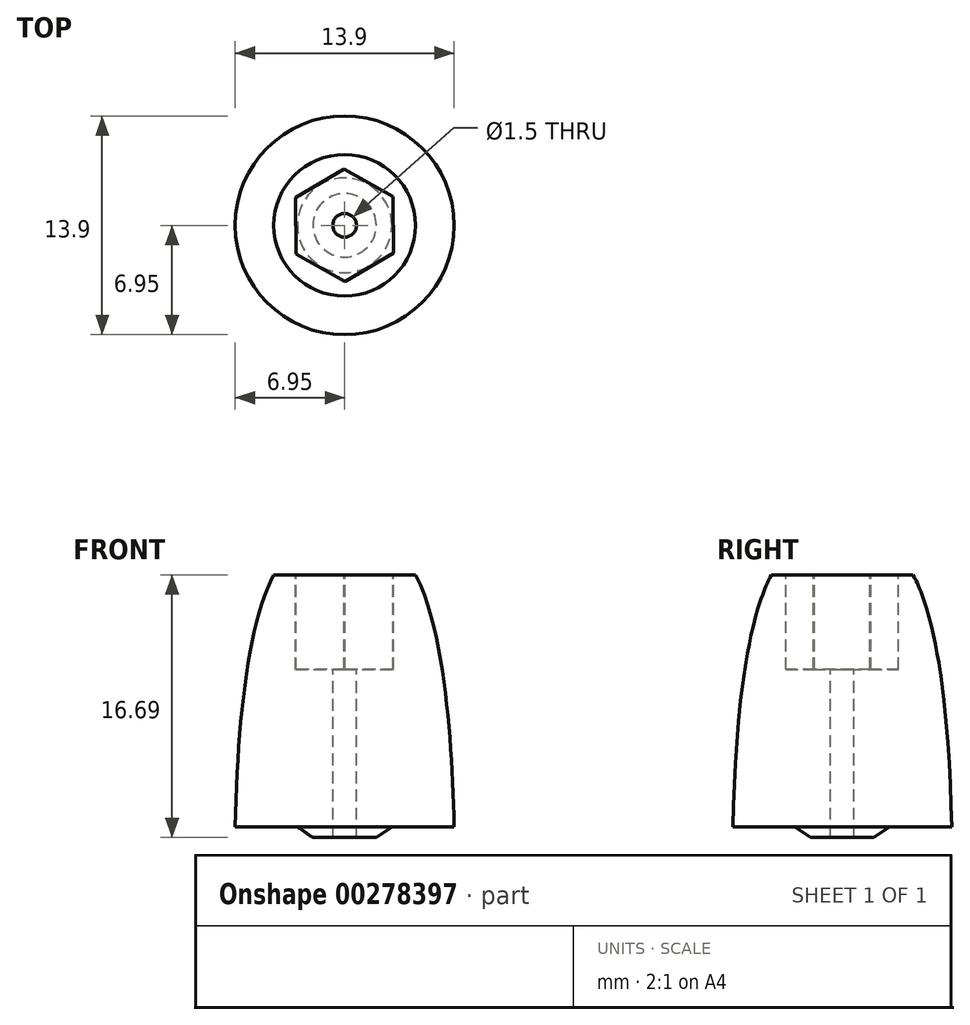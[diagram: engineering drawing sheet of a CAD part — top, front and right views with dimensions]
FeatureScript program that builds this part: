
annotation { "Feature Type Name" : "Feature", "Feature Type Description" : "" }
export const myFeature = defineFeature(function(context is Context, id is Id, definition is map)
    precondition{}
    {
        {
            var Q0;
            Q0=qCreatedBy(makeId("Front.planeOp"),FACE);
            var sketch = newSketch(context, id + "F0", { "sketchPlane" : qUnion([Q0])});
            skLineSegment(sketch, "E0", {"start": v(0, 0) * mm, "end": v(0, 16) * mm});
            skLineSegment(sketch, "E1", {"start": v(0, 16) * mm, "end": v(-4.5, 16) * mm});
            skLineSegment(sketch, "E2", {"start": v(-3, 0) * mm, "end": v(-6.95, 0) * mm});
            skFitSpline(sketch, "E3", {"points": [v(-4.5, 16) * mm, v(-6.95, 0) * mm], "startDerivative": vector(-4.94, -9.17) * mm, "endDerivative": vector(-0.43, -19.85) * mm});
            skLineSegment(sketch, "E4", {"start": v(-3, 0) * mm, "end": v(-2.01, -0.7) * mm});
            skLineSegment(sketch, "E5", {"start": v(-2.01, -0.7) * mm, "end": v(0, -0.7) * mm});
            skLineSegment(sketch, "E6", {"start": v(0, -0.7) * mm, "end": v(0, 0) * mm});
            skSolve(sketch);
        }
        {
            var Q0;
            Q0=makeQuery(id+"F0.imprint","IMPRINT",FACE,{"disambiguationData":[TD([[makeQuery(id+"F0.imprint","IMPRINT",EDGE,{"derivedFrom":sQuery(id+"F0.wireOp",EDGE,"E0")}),1.0]])]});
            var Q1;
            Q1=sQuery(id+"F0.wireOp",EDGE,"E0");
            revolve(context, id + "F1", {"entities" : qUnion([Q0]), "axis" : qUnion([Q1]), "revolveType" : RevolveType.FULL});
        }
        {
            var Q0;
            Q0=makeQuery(id+"F1.opRevolve","SWEPT_FACE",FACE,{"disambiguationData":[OSD([sQuery(id+"F0.wireOp",EDGE,"E1")])]});
            var sketch = newSketch(context, id + "F2", { "sketchPlane" : qUnion([Q0])});
            skCircle(sketch, "E7.cCircle", {"center": v(0, 0) * mm, "radius": 3.1 * mm, "construction": true});
            skLineSegment(sketch, "E7.0", {"start": v(-3.12, 1.76) * mm, "end": v(-0.04, 3.58) * mm});
            skLineSegment(sketch, "E7.1", {"start": v(-0.04, 3.58) * mm, "end": v(3.08, 1.82) * mm});
            skLineSegment(sketch, "E7.2", {"start": v(3.08, 1.82) * mm, "end": v(3.12, -1.76) * mm});
            skLineSegment(sketch, "E7.3", {"start": v(3.12, -1.76) * mm, "end": v(0.04, -3.58) * mm});
            skLineSegment(sketch, "E7.4", {"start": v(0.04, -3.58) * mm, "end": v(-3.08, -1.82) * mm});
            skLineSegment(sketch, "E7.5", {"start": v(-3.08, -1.82) * mm, "end": v(-3.12, 1.76) * mm});
            skPoint(sketch, "E7.0.midPoint", {"position": v(-1.58, 2.67) * mm});
            skSolve(sketch);
        }
        {
            var Q0;
            Q0 = qSketchRegion(id + "F2", true);
            extrude(context, id + "F3", {"entities" : qUnion([Q0]), "operationType" : NewBodyOperationType.REMOVE, "oppositeDirection" : true, "depth" : 6 * mm});
        }
        {
            var Q0;
            Q0=makeQuery(id+"F3.boolean.opBoolean","COPY",FACE,{"derivedFrom":makeQuery(id+"F3.opExtrude","CAP_FACE",FACE,{"disambiguationData":[OSD([sQuery(id+"F2.wireOp",EDGE,"E7.0"),sQuery(id+"F2.wireOp",EDGE,"E7.1"),sQuery(id+"F2.wireOp",EDGE,"E7.2"),sQuery(id+"F2.wireOp",EDGE,"E7.3"),sQuery(id+"F2.wireOp",EDGE,"E7.4"),sQuery(id+"F2.wireOp",EDGE,"E7.5")])],"isStart":false})});
            var sketch = newSketch(context, id + "F4", { "sketchPlane" : qUnion([Q0])});
            skCircle(sketch, "E8", {"center": v(0, 0) * mm, "radius": 0.75 * mm});
            skSolve(sketch);
        }
        {
            var Q0;
            Q0 = qSketchRegion(id + "F4", true);
            extrude(context, id + "F5", {"entities" : qUnion([Q0]), "operationType" : NewBodyOperationType.REMOVE, "endBound" : BoundingType.THROUGH_ALL, "oppositeDirection" : true, "depth" : 25 * mm});
        }
    });
